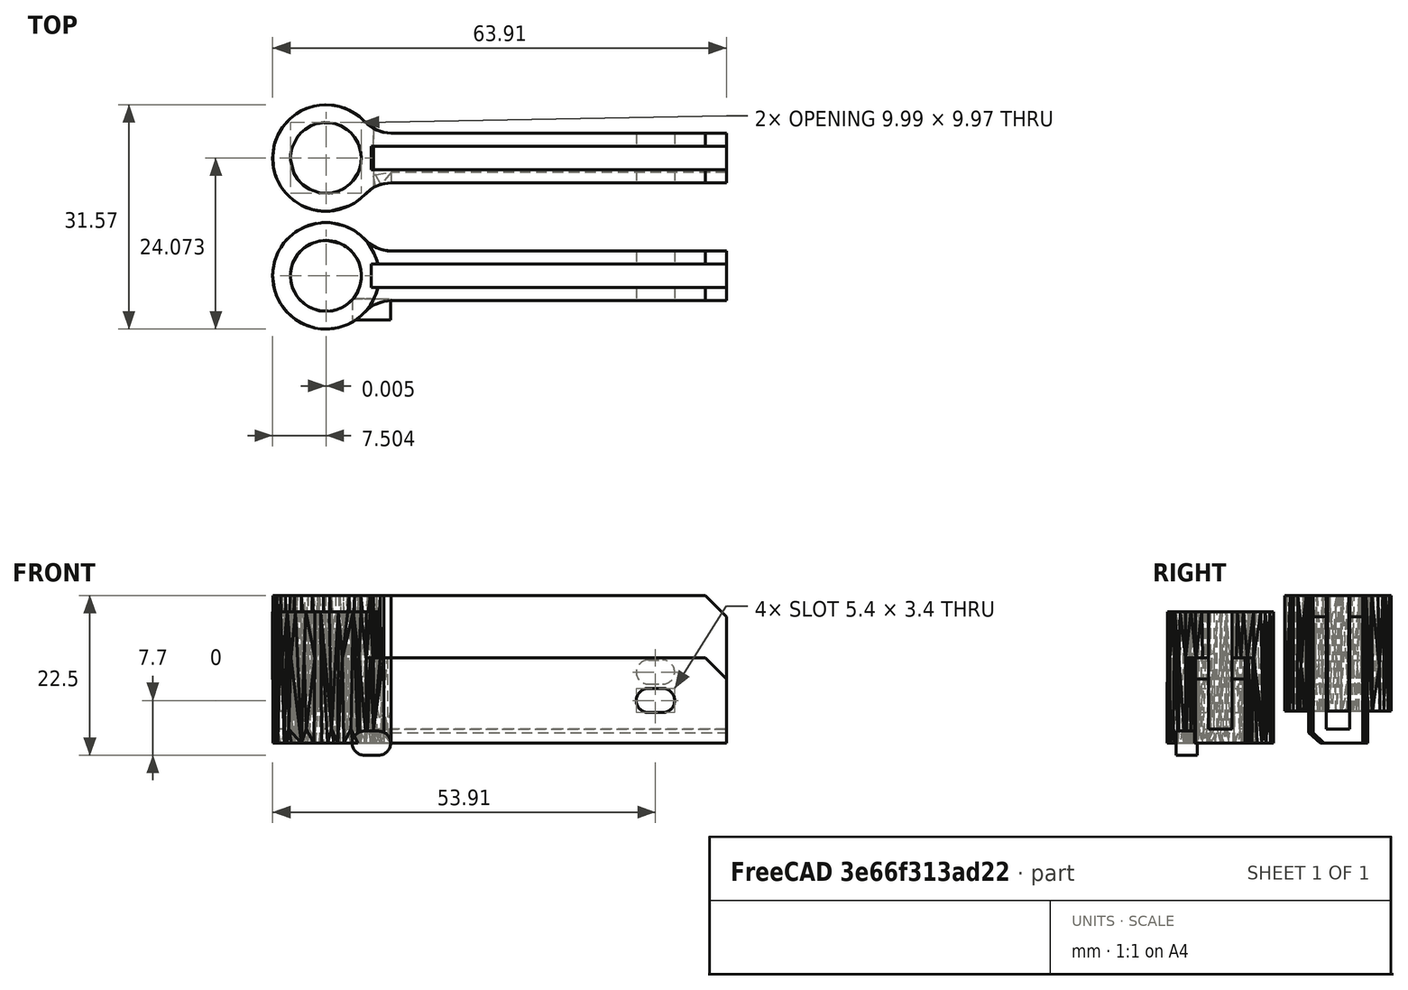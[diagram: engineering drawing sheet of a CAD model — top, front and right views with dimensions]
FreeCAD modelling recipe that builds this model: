
FCSTD DOCUMENT  (FreeCAD 0.18R16146 (Git))
Label: hingle-drill
License: All rights reserved
LicenseURL: http://en.wikipedia.org/wiki/All_rights_reserved
objects: Part::Feature×6, Part::Cut×6, Part::Box×3, Part::Cylinder×2, Part::MultiFuse×1
note: 18 computed .brp shape members not serialized (recipe doc carries the construction recipe); baked Part::Feature solids carry a one-line shape summary decoded from their .brp

FEATURE [Part::Feature] top_handle001001_solid  label="top_handle002 (Solid)"
  Placement = pos=(0,-30.81,0) rot=(0,0,1;0rad)
  shape: bbox 63.91 x 14.98 x 18.5 mm, 326 faces (baked)
FEATURE [Part::Feature] bottom_handle001001_solid  label="bottom_handle002 (Solid)"
  Placement = pos=(0,-61.62,0) rot=(0,0,1;0rad)
  shape: bbox 63.91 x 14.99 x 20.8 mm, 256 faces (baked)
FEATURE [Part::Box] Box  label="Cube"
  AttacherType = Attacher::AttachEngine3D
  Height = 21
  Length = 51
  Placement = pos=(-44.76,1.58,2) rot=(0,0,1;0rad)
  Width = 3.3
FEATURE [Part::Box] Box001  label="Cube001"
  AttacherType = Attacher::AttachEngine3D
  Height = 18.8
  Length = 61
  Placement = pos=(10.75,2.16,0) rot=(0,0,1;0rad)
  Width = 3.3
FEATURE [Part::Cut] Cut001  label="bottom"
  Base = -> bottom_handle001001_solid
  Placement = pos=(71.75,2.2e-14,20.8) rot=(0,1,0;3.14159rad)
  Tool = -> Box001
FEATURE [Part::Cylinder] Cylinder
  Angle = 360
  AttacherType = Attacher::AttachEngine3D
  Height = 3
  Placement = pos=(-1,0,0) rot=(1,0,0;1.5708rad)
  Radius = 1.7
FEATURE [Part::Cylinder] Cylinder001
  Angle = 360
  AttacherType = Attacher::AttachEngine3D
  Height = 3
  Placement = pos=(1,0,0) rot=(1,0,0;1.5708rad)
  Radius = 1.7
FEATURE [Part::Box] Box002  label="Cube002"
  AttacherType = Attacher::AttachEngine3D
  Height = 3.4
  Length = 2
  Placement = pos=(-1,-3,-1.7) rot=(0,0,1;0rad)
  Width = 3
FEATURE [Part::MultiFuse] Fusion  label="hole-range"
  Shapes = -> [Box002,Cylinder,Cylinder001]
FEATURE [Part::Feature] Fusion001  label="hole-range001"
  Placement = pos=(40,8,10) rot=(0,0,1;0rad)
  shape: bbox 5.4 x 3 x 3.4 mm, 6 faces (baked)
FEATURE [Part::Cut] Cut  label="top"
  Base = -> top_handle001001_solid
  Placement = pos=(44.76,0,0) rot=(0,0,1;0rad)
  Tool = -> Box
FEATURE [Part::Feature] Fusion002  label="hole-range002"
  Placement = pos=(40,2,6) rot=(0,0,1;0rad)
  shape: bbox 5.4 x 3 x 3.4 mm, 6 faces (baked)
FEATURE [Part::Feature] Fusion001001  label="hole-range003"
  Placement = pos=(40,3,10) rot=(0,0,1;0rad)
  shape: bbox 5.4 x 3 x 3.4 mm, 6 faces (baked)
FEATURE [Part::Cut] Cut004
  Base = -> Cut001
  Tool = -> Fusion001001
FEATURE [Part::Cut] Cut005
  Base = -> Cut004
  Placement = pos=(0,16,0) rot=(0,0,1;0rad)
  Tool = -> Fusion001
FEATURE [Part::Feature] Fusion002001  label="hole-range004"
  Placement = pos=(40,7,6) rot=(0,0,1;0rad)
  shape: bbox 5.4 x 3 x 3.4 mm, 6 faces (baked)
FEATURE [Part::Cut] Cut006
  Base = -> Cut
  Tool = -> Fusion002001
FEATURE [Part::Cut] Cut007
  Base = -> Cut006
  Tool = -> Fusion002
